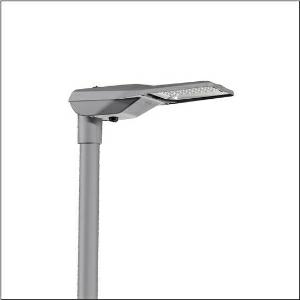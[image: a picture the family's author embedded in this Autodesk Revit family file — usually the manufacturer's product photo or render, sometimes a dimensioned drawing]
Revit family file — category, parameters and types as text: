
# Revit family: streetlight_sl_21_mini___p0_5a_5xe2v33t08hb_c971
name_source: partatom
category: Lighting Fixtures
units: mm (PartAtom-declared; Revit-internal decimal feet)

## family parameters
Cut with Voids When Loaded = No
Host = Face
Light Source = No
Part Type = Normal
Room Calculation Point = No
Round Connector Dimension = Use Diameter
Shared = No

## types (1)
- --- (1 x LED, 8890 lm, 66 W, 3000K)
    Apparent Load = 66 VA
    CIE Flux Codes = 37 73 96 100 100
    Color Rendering = 70
    Color Temperature = 3000K
    Default Elevation = 1800 mm
    Description = Streetlight SL 21 mini, mast luminaire, primary light control with lens, of PMMA, primary optical cover: cover, of toughened safety glass, transparent, light distribution: P0.5a, light emission: direct distribution, primary light characteristic: asymmetric, installation type: post-top, side-entry, LED, High Power LED, rated luminous flux: 8.890lm, luminous efficacy: 135lm/W, light colour: 730, colour temperature: 3000K, control gear: D4i, control: pre-setting: logarithmic dimming characteristic, flexible luminous flux parameterisation, time-dependent luminous flux control, constant luminous flux control, overheat protection, mains connection: 220..240V, AC, 50/60Hz, start of lifetime: 66W, end of service life: 69W, reduction: 30W, luminaire housing, of diecast aluminium, powder-coated, Siteco® metallic grey (DB 702S), corrosivity category C5 mid according to DIN EN ISO 12944, multi-level sealing system, sealing non-destructively replaceable, inclination adjustable: 0°, 5°, 10°, 15°, please order mast flange separately, length: 628mm, width: 235mm, height: 110mm, mast flange for spigot size: 42mm (side-entry): 5XC10008XM4, 60/48mm (side-entry/post-top): 5XC10108XM2, 76/60mm (side-entry/post-top): 5XC10108XM1, mounting height: 4..8m, Smart Interface below and above, protection rating (complete): IP66, insulation class (complete): insulation class II (safety insulation), certification: CE, ENEC, ENEC+, VDE, impact resistance: IK10, permissible operating ambient temperature for outdoor applications: -40..+50°C, standard-compliant lighting for roads and squares, packaging unit: 1 piece

Light Distribution: P0.5a
    Height = 110 mm
    Lamp = 1 x LED
    Lamp Light Flux = 8890 lm
    Lamp Power = 66 W
    Lamp count = 1
    Length = 625 mm
    Luminous efficacy = 135 lm/W
    Manufacturer = Siteco
    ModVariant = No
    Model = 5XE2V33T08HB
    Number of Poles = 1
    OnlyDefault = Yes
    Power Factor = 1
    Product Name = Streetlight SL 21 mini | P0.5a
    Product group = mast luminaire | pylon top
    ProductGroupID = 6100
    Protection Class = Protection class II
    Protection Degree = IP 66
    RLX_Detail_Level = 1
    RLX_Emergency_Light_Flux = 0 lm
    RLX_Emergency_Type = 0
    RLX_Emergency_Type_DB = No
    RlxData = <blob elided: 93237 chars, md5=f26ab8ca>
    Socket = socket
    Standby Power = 0 W
    System Light Flux = 8890 lm
    System Power = 66 W
    Type Comments = factory setting: luminous flux: 100 % | dim-lin: 254 | 670 mA
    Type Image = l_1003514.jpg
    URL = http://relux.com
    VarID = @adj_091291
    Voltage = 0 V
    Weight = 0.00 kg
    Width = 234 mm

## geometry (parser evidence)
native form markers: Blend x4, Sweep x11
no freeform markers — native parametric forms only
